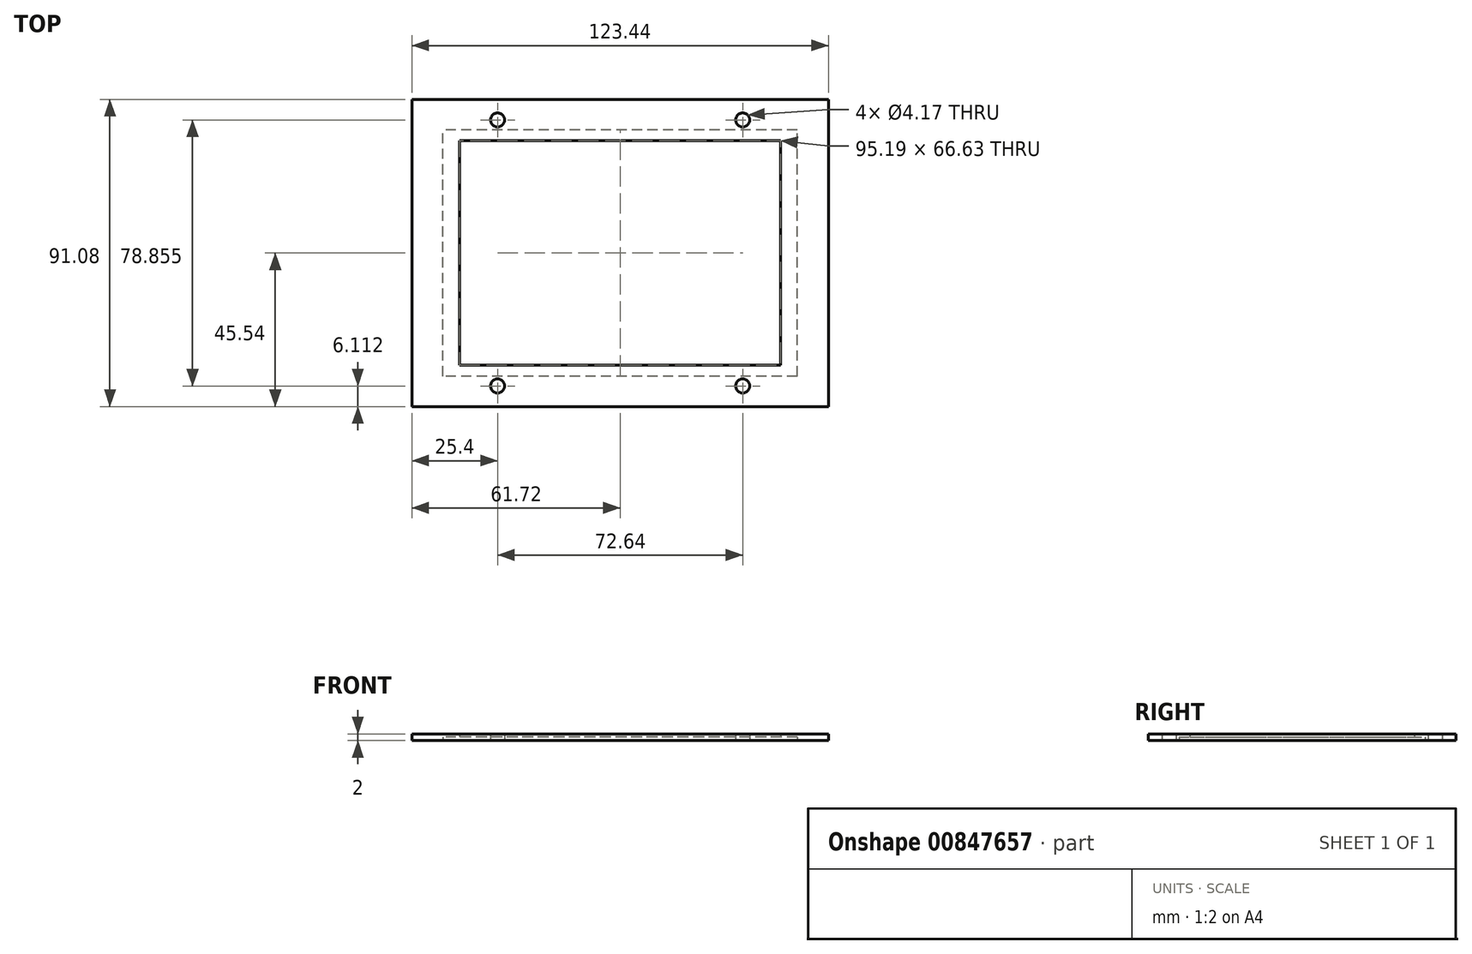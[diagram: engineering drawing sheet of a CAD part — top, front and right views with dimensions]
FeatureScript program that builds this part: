
annotation { "Feature Type Name" : "Feature", "Feature Type Description" : "" }
export const myFeature = defineFeature(function(context is Context, id is Id, definition is map)
    precondition{}
    {
        {
            var Q0;
            Q0=qCreatedBy(makeId("Top.planeOp"),FACE);
            var sketch = newSketch(context, id + "F0", { "sketchPlane" : qUnion([Q0])});
            skLineSegment(sketch, "E0.bottom", {"start": v(61.72, -45.54) * mm, "end": v(-61.72, -45.54) * mm});
            skLineSegment(sketch, "E0.top", {"start": v(61.72, 45.54) * mm, "end": v(-61.72, 45.54) * mm});
            skLineSegment(sketch, "E0.left", {"start": v(61.72, -45.54) * mm, "end": v(61.72, 45.54) * mm});
            skLineSegment(sketch, "E0.right", {"start": v(-61.72, -45.54) * mm, "end": v(-61.72, 45.54) * mm});
            skPoint(sketch, "E0.middle", {"position": v(0, 0) * mm});
            skLineSegment(sketch, "E1.bottom", {"start": v(47.6, -33.32) * mm, "end": v(-47.6, -33.32) * mm});
            skLineSegment(sketch, "E1.top", {"start": v(47.6, 33.32) * mm, "end": v(-47.6, 33.32) * mm});
            skLineSegment(sketch, "E1.left", {"start": v(47.6, -33.32) * mm, "end": v(47.6, 33.32) * mm});
            skLineSegment(sketch, "E1.right", {"start": v(-47.6, -33.32) * mm, "end": v(-47.6, 33.32) * mm});
            skLineSegment(sketch, "E2", {"start": v(-36.32, 45.54) * mm, "end": v(-36.32, 33.32) * mm});
            skCircle(sketch, "E3", {"center": v(-36.32, 39.43) * mm, "radius": 2.08 * mm});
            skCircle(sketch, "E4", {"center": v(36.32, 39.43) * mm, "radius": 2.08 * mm});
            skCircle(sketch, "E5", {"center": v(36.32, -39.43) * mm, "radius": 2.08 * mm});
            skLineSegment(sketch, "E6", {"start": v(36.32, -33.32) * mm, "end": v(36.32, -45.54) * mm, "construction": true});
            skCircle(sketch, "E7", {"center": v(-36.32, -39.43) * mm, "radius": 2.08 * mm});
            skSolve(sketch);
        }
        {
            var Q0;
            Q0 = qSketchRegion(id + "F0", true);
            extrude(context, id + "F1", {"entities" : qUnion([Q0]), "depth" : 2 * mm, "offsetDistance" : 25.4 * mm});
        }
        {
            var Q0;
            Q0=qCreatedBy(makeId("Top.planeOp"),FACE);
            var sketch = newSketch(context, id + "F2", { "sketchPlane" : qUnion([Q0])});
            skLineSegment(sketch, "E8.bottom", {"start": v(52.5, -36.5) * mm, "end": v(-52.5, -36.5) * mm});
            skLineSegment(sketch, "E8.top", {"start": v(52.5, 36.5) * mm, "end": v(-52.5, 36.5) * mm});
            skLineSegment(sketch, "E8.left", {"start": v(52.5, -36.5) * mm, "end": v(52.5, 36.5) * mm});
            skLineSegment(sketch, "E8.right", {"start": v(-52.5, -36.5) * mm, "end": v(-52.5, 36.5) * mm});
            skPoint(sketch, "E8.middle", {"position": v(0, 0) * mm});
            skSolve(sketch);
        }
        {
            var Q0;
            Q0 = qSketchRegion(id + "F2", true);
            extrude(context, id + "F3", {"entities" : qUnion([Q0]), "operationType" : NewBodyOperationType.REMOVE, "depth" : 1 * mm, "offsetDistance" : 25.4 * mm});
        }
    });
